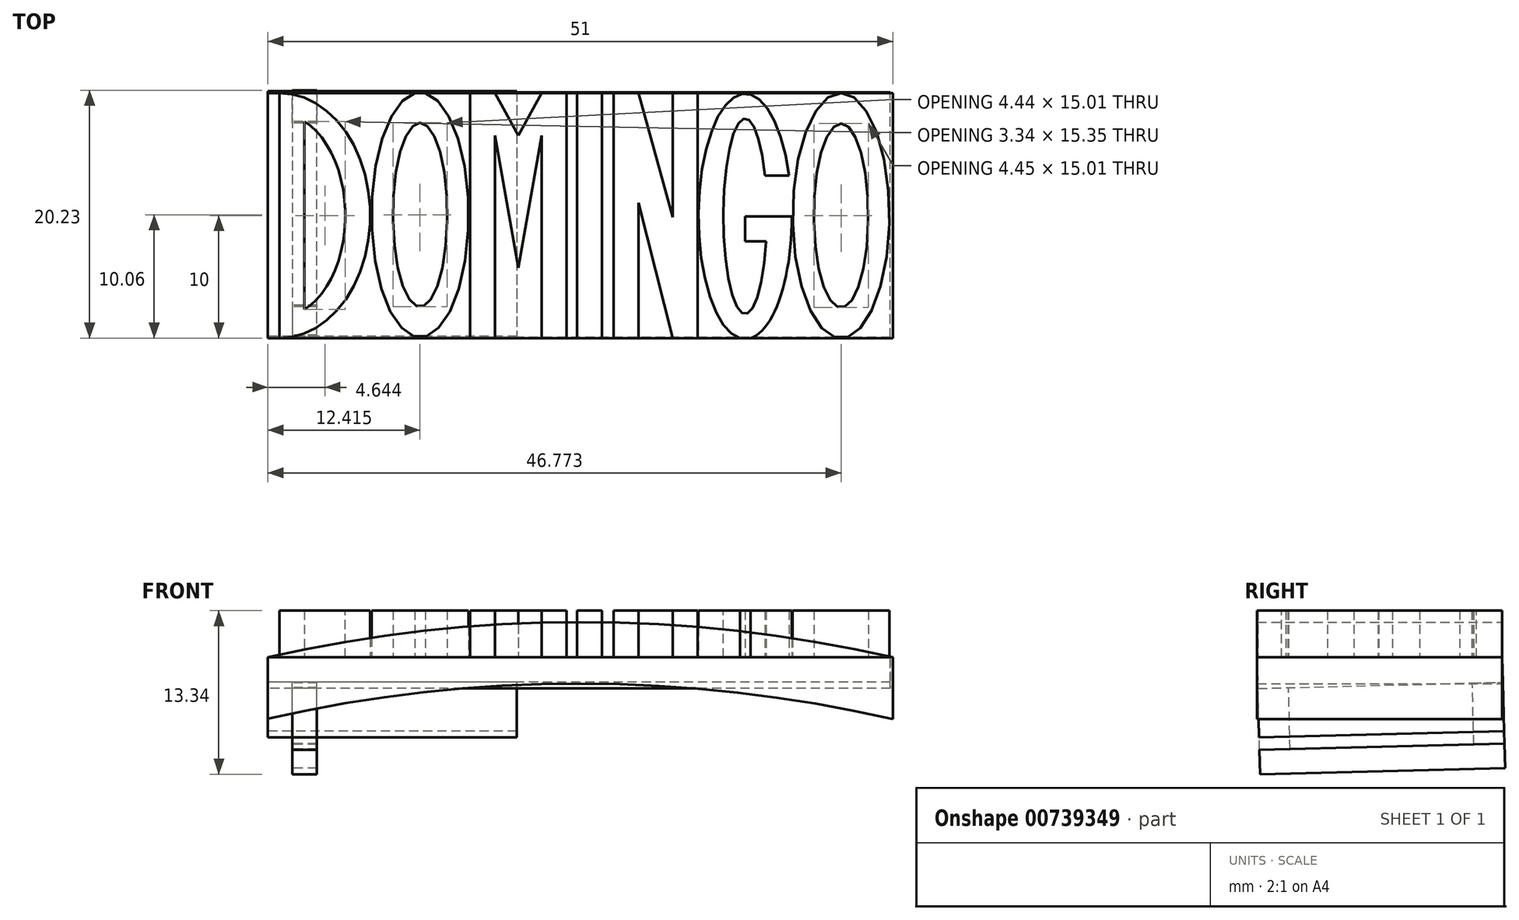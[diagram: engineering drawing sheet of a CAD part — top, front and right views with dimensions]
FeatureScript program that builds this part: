
annotation { "Feature Type Name" : "Feature", "Feature Type Description" : "" }
export const myFeature = defineFeature(function(context is Context, id is Id, definition is map)
    precondition{}
    {
        {
            var Q0;
            Q0=qCreatedBy(makeId("Front.planeOp"),FACE);
            var sketch = newSketch(context, id + "F0", { "sketchPlane" : qUnion([Q0])});
            skArc(sketch, "E0", {"start": v(21, 27.83) * mm, "mid": v(-4.5, 30.73) * mm, "end": v(-30, 27.87) * mm});
            skLineSegment(sketch, "E1", {"start": v(-30, 27.87) * mm, "end": v(-30, 32.87) * mm});
            skLineSegment(sketch, "E2", {"start": v(21, 27.83) * mm, "end": v(21, 32.87) * mm});
            skArc(sketch, "E3", {"start": v(21, 32.87) * mm, "mid": v(-4.5, 35.75) * mm, "end": v(-30, 32.87) * mm});
            skSolve(sketch);
        }
        {
            var Q0;
            Q0=makeQuery(id+"F0.imprint","IMPRINT",FACE,{"disambiguationData":[TD([[makeQuery(id+"F0.imprint","IMPRINT",EDGE,{"derivedFrom":sQuery(id+"F0.wireOp",EDGE,"E0")}),-1.0]])]});
            extrude(context, id + "F1", {"entities" : qUnion([Q0]), "depth" : 20 * mm, "offsetDistance" : 25.4 * mm});
        }
        {
            var Q0;
            Q0=qCreatedBy(makeId("Top.planeOp"),FACE);
            var sketch = newSketch(context, id + "F2", { "sketchPlane" : qUnion([Q0])});
            skLineSegment(sketch, "E4", {"start": v(-23.33, 11.9) * mm, "end": v(-23.33, 4.28) * mm});
            skArc(sketch, "E5", {"start": v(-23.33, 4.28) * mm, "mid": v(-19.37, 8.09) * mm, "end": v(-23.33, 11.9) * mm});
            skSolve(sketch);
        }
        {
            var Q0;
            Q0=makeQuery(id+"F2.imprint","IMPRINT",FACE,{"disambiguationData":[TD([[makeQuery(id+"F2.imprint","IMPRINT",EDGE,{"derivedFrom":sQuery(id+"F2.wireOp",EDGE,"E4")}),1.0]])]});
            extrude(context, id + "F3", {"entities" : qUnion([Q0]), "depth" : 5.08 * mm, "offsetDistance" : 25.4 * mm});
        }
        {
            var Q0;
            Q0=makeQuery(id+"F1.opExtrude","SWEPT_FACE",FACE,{"disambiguationData":[OSD([sQuery(id+"F0.wireOp",EDGE,"E1")])]});
            var sketch = newSketch(context, id + "F4", { "sketchPlane" : qUnion([Q0])});
            skLineSegment(sketch, "E6", {"start": v(20, 32.87) * mm, "end": v(19.94, 30.33) * mm});
            skLineSegment(sketch, "E7", {"start": v(19.94, 30.33) * mm, "end": v(-0.05, 30.84) * mm});
            skLineSegment(sketch, "E8", {"start": v(-0.05, 30.84) * mm, "end": v(0, 32.87) * mm});
            skLineSegment(sketch, "E9", {"start": v(0, 32.87) * mm, "end": v(20, 32.87) * mm});
            skSolve(sketch);
        }
        {
            var Q0;
            Q0 = qSketchRegion(id + "F4", true);
            extrude(context, id + "F5", {"entities" : qUnion([Q0]), "oppositeDirection" : true, "depth" : 50.8 * mm, "offsetDistance" : 25.4 * mm});
        }
        {
            var Q0;
            Q0=makeQuery(id+"F5.opExtrude","SWEPT_FACE",FACE,{"disambiguationData":[OSD([sQuery(id+"F4.wireOp",EDGE,"E9")])]});
            var sketch = newSketch(context, id + "F6", { "sketchPlane" : qUnion([Q0])});
            skLineSegment(sketch, "E10", {"start": v(-29.06, 0) * mm, "end": v(-29.06, -20) * mm});
            skEllipse(sketch, "E11", {"center": v(-29.06, -10) * mm, "majorRadius": 10 * mm, "minorRadius": 7.4 * mm, "majorAxis": v(0, -1)});
            skLineSegment(sketch, "E12", {"start": v(-27.02, -2.33) * mm, "end": v(-27.02, -17.7) * mm});
            skEllipse(sketch, "E13", {"center": v(-29.06, -10) * mm, "majorRadius": 5.37 * mm, "minorRadius": 8.3 * mm, "majorAxis": v(1, 0)});
            skLineSegment(sketch, "E14", {"start": v(-23.69, -10) * mm, "end": v(-21.66, -10) * mm});
            skSolve(sketch);
        }
        {
            var Q0;
            {var subQ0=sQuery(id+"F6.wireOp",EDGE,"E10");Q0=makeQuery(id+"F6.imprint","IMPRINT",FACE,{"disambiguationData":[TD([[makeQuery(id+"F6.imprint","IMPRINT",EDGE,{"derivedFrom":subQ0}),1.0]])]});}
            var Q1;
            {var subQ4=sQuery(id+"F6.wireOp",EDGE,"E12");Q1=makeQuery(id+"F6.imprint","IMPRINT",FACE,{"disambiguationData":[TD([[makeQuery(id+"F6.imprint","IMPRINT",EDGE,{"derivedFrom":subQ4}),-1.0]])]});}
            var Q2;
            {var subQ2=sQuery(id+"F6.wireOp",EDGE,"zUHBSBTi-NJOX-96SZ-FGQs-dRdukynPxQgg");Q2=makeQuery(id+"F6.imprint","IMPRINT",FACE,{"disambiguationData":[TD([[makeQuery(id+"F6.imprint","IMPRINT",EDGE,{"derivedFrom":subQ2}),1.0]])]});}
            var Q3;
            {var subQ0=sQuery(id+"F6.wireOp",EDGE,"zUHBSBTi-NJOX-96SZ-FGQs-dRdukynPxQgg");Q3=makeQuery(id+"F6.imprint","IMPRINT",FACE,{"disambiguationData":[TD([[makeQuery(id+"F6.imprint","IMPRINT",EDGE,{"derivedFrom":subQ0}),-1.0]])]});}
            var Q4;
            {var subQ2=sQuery(id+"F6.wireOp",EDGE,"E14");Q4=makeQuery(id+"F6.imprint","IMPRINT",FACE,{"disambiguationData":[TD([[makeQuery(id+"F6.imprint","IMPRINT",EDGE,{"derivedFrom":subQ2}),1.0]])]});}
            var Q5;
            {var subQ0=sQuery(id+"F6.wireOp",EDGE,"E14");Q5=makeQuery(id+"F6.imprint","IMPRINT",FACE,{"disambiguationData":[TD([[makeQuery(id+"F6.imprint","IMPRINT",EDGE,{"derivedFrom":subQ0}),-1.0]])]});}
            extrude(context, id + "F7", {"entities" : qUnion([Q0, Q1, Q2, Q3, Q4, Q5]), "depth" : 3.8 * mm, "offsetDistance" : 25.4 * mm});
        }
        {
            var Q0;
            Q0=makeQuery(id+"F7.opExtrude","SWEPT_BODY",BODY,{"disambiguationData":[OSD([sQuery(id+"F6.wireOp",EDGE,"E10"),sQuery(id+"F6.wireOp",EDGE,"E11")])]});
            transform(context, id + "F8", {"entities" : qUnion([Q0]), "transformType" : TransformType.TRANSLATION_3D, "dx" : 9.37 * mm, "dy" : -0.15 * mm, "dz" : 0 * mm, "makeCopy" : true});
        }
        {
            var Q0;
            Q0=makeQuery(id+"F8.opPattern","COPY",BODY,{"derivedFrom":makeQuery(id+"F7.opExtrude","SWEPT_BODY",BODY,{"disambiguationData":[OSD([sQuery(id+"F6.wireOp",EDGE,"E10"),sQuery(id+"F6.wireOp",EDGE,"E11")])]}),"instanceName":"1"});
            deleteBodies(context, id + "F9", {"entities" : qUnion([Q0])});
        }
        {
            var Q0;
            Q0=makeQuery(id+"F5.opExtrude","SWEPT_FACE",FACE,{"disambiguationData":[OSD([sQuery(id+"F4.wireOp",EDGE,"E7")])]});
            var sketch = newSketch(context, id + "F10", { "sketchPlane" : qUnion([Q0])});
            skLineSegment(sketch, "E15", {"start": v(-28, 19.17) * mm, "end": v(-26, 19.17) * mm});
            skLineSegment(sketch, "E16", {"start": v(-26, 19.17) * mm, "end": v(-26, 16.67) * mm});
            skLineSegment(sketch, "E17", {"start": v(-26, 16.67) * mm, "end": v(-28, 16.67) * mm});
            skLineSegment(sketch, "E18", {"start": v(-28, 16.67) * mm, "end": v(-28, 19.17) * mm});
            skLineSegment(sketch, "E19", {"start": v(-28, 1.67) * mm, "end": v(-28, -0.83) * mm});
            skLineSegment(sketch, "E20", {"start": v(-28, -0.83) * mm, "end": v(-26, -0.83) * mm});
            skLineSegment(sketch, "E21", {"start": v(-26, -0.83) * mm, "end": v(-26, 1.67) * mm});
            skLineSegment(sketch, "E22", {"start": v(-26, 1.67) * mm, "end": v(-28, 1.67) * mm});
            skLineSegment(sketch, "E23", {"start": v(-26, 1.67) * mm, "end": v(-26, 16.67) * mm});
            skLineSegment(sketch, "E24", {"start": v(-28, 1.67) * mm, "end": v(-28, 16.67) * mm});
            skSolve(sketch);
        }
        {
            var Q0;
            Q0=makeQuery(id+"F10.imprint","IMPRINT",FACE,{"disambiguationData":[TD([[makeQuery(id+"F10.imprint","IMPRINT",EDGE,{"derivedFrom":sQuery(id+"F10.wireOp",EDGE,"E15")}),1.0]])]});
            var Q1;
            Q1=makeQuery(id+"F10.imprint","IMPRINT",FACE,{"disambiguationData":[TD([[makeQuery(id+"F10.imprint","IMPRINT",EDGE,{"derivedFrom":sQuery(id+"F10.wireOp",EDGE,"E19")}),1.0]])]});
            extrude(context, id + "F11", {"entities" : qUnion([Q0, Q1]), "depth" : 5 * mm, "offsetDistance" : 25.4 * mm});
        }
        {
            var Q0;
            Q0=makeQuery(id+"F11.opExtrude","CAP_FACE",FACE,{"disambiguationData":[OSD([sQuery(id+"F10.wireOp",EDGE,"E15"),sQuery(id+"F10.wireOp",EDGE,"E16"),sQuery(id+"F10.wireOp",EDGE,"E17"),sQuery(id+"F10.wireOp",EDGE,"E18")])],"isStart":false});
            var sketch = newSketch(context, id + "F12", { "sketchPlane" : qUnion([Q0])});
            skLineSegment(sketch, "E25", {"start": v(-26, 19.17) * mm, "end": v(-26, -0.83) * mm});
            skLineSegment(sketch, "E26", {"start": v(-26, -0.83) * mm, "end": v(-28, -0.83) * mm});
            skLineSegment(sketch, "E27", {"start": v(-28, -0.83) * mm, "end": v(-28, 19.17) * mm});
            skLineSegment(sketch, "E28", {"start": v(-28, 19.17) * mm, "end": v(-26, 19.17) * mm});
            skSolve(sketch);
        }
        {
            var Q0;
            {var subQ2=sQuery(id+"F12.wireOp",EDGE,"E26");Q0=makeQuery(id+"F12.imprint","IMPRINT",FACE,{"disambiguationData":[TD([[makeQuery(id+"F12.imprint","IMPRINT",EDGE,{"derivedFrom":subQ2}),-1.0]])]});}
            var Q1;
            {var subQ0=sQuery(id+"F12.wireOp",EDGE,"E28");Q1=makeQuery(id+"F12.imprint","IMPRINT",FACE,{"disambiguationData":[TD([[makeQuery(id+"F12.imprint","IMPRINT",EDGE,{"derivedFrom":subQ0}),1.0]])]});}
            extrude(context, id + "F13", {"entities" : qUnion([Q0, Q1]), "depth" : 2 * mm, "offsetDistance" : 25.4 * mm});
        }
        {
            var Q0;
            Q0=makeQuery(id+"F3.opExtrude","SWEPT_BODY",BODY,{"disambiguationData":[OSD([sQuery(id+"F2.wireOp",EDGE,"E4"),sQuery(id+"F2.wireOp",EDGE,"E5")])]});
            deleteBodies(context, id + "F14", {"entities" : qUnion([Q0])});
        }
        {
            var Q0;
            {var subQ2=sQuery(id+"F4.wireOp",EDGE,"E9");var subQ7=makeQuery(id+"F5.opExtrude","CAP_EDGE",EDGE,{"disambiguationData":[OSD([subQ2])],"isStart":false});Q0=makeQuery(id+"F6.imprint","IMPRINT",FACE,{"disambiguationData":[TD([[makeQuery(id+"F6.imprint","IMPRINT",EDGE,{"derivedFrom":subQ7}),1.0]])]});}
            var sketch = newSketch(context, id + "F15", { "sketchPlane" : qUnion([Q0])});
            skEllipse(sketch, "E29", {"center": v(-17.59, -9.94) * mm, "majorRadius": 10 * mm, "minorRadius": 3.95 * mm, "majorAxis": v(0, 1)});
            skEllipse(sketch, "E30", {"center": v(-17.59, -9.94) * mm, "majorRadius": 7.5 * mm, "minorRadius": 2.22 * mm, "majorAxis": v(0, 1)});
            skSolve(sketch);
        }
        {
            var Q0;
            Q0=makeQuery(id+"F15.imprint","IMPRINT",FACE,{"disambiguationData":[TD([[makeQuery(id+"F15.imprint","IMPRINT",EDGE,{"derivedFrom":sQuery(id+"F15.wireOp",EDGE,"E30")}),-1.0]])]});
            extrude(context, id + "F16", {"entities" : qUnion([Q0]), "depth" : 3.8 * mm, "offsetDistance" : 25.4 * mm});
        }
        {
            var Q0;
            Q0=makeQuery(id+"F5.opExtrude","SWEPT_FACE",FACE,{"disambiguationData":[OSD([sQuery(id+"F4.wireOp",EDGE,"E9")])]});
            var sketch = newSketch(context, id + "F17", { "sketchPlane" : qUnion([Q0])});
            skLineSegment(sketch, "E31", {"start": v(-13.5, 0) * mm, "end": v(-13.5, -20) * mm});
            skLineSegment(sketch, "E32", {"start": v(-13.5, -20) * mm, "end": v(-11.47, -20) * mm});
            skLineSegment(sketch, "E33", {"start": v(-11.47, -20) * mm, "end": v(-11.47, -3.47) * mm});
            skLineSegment(sketch, "E34", {"start": v(-11.47, -3.47) * mm, "end": v(-9.56, -14.27) * mm});
            skLineSegment(sketch, "E35", {"start": v(-9.56, -14.27) * mm, "end": v(-7.66, -3.47) * mm});
            skLineSegment(sketch, "E36", {"start": v(-7.66, -3.47) * mm, "end": v(-7.66, -20) * mm});
            skLineSegment(sketch, "E37", {"start": v(-7.66, -20) * mm, "end": v(-5.62, -20) * mm});
            skLineSegment(sketch, "E38", {"start": v(-5.62, -20) * mm, "end": v(-5.62, 0) * mm});
            skLineSegment(sketch, "E39", {"start": v(-5.62, 0) * mm, "end": v(-7.66, 0) * mm});
            skLineSegment(sketch, "E40", {"start": v(-7.66, 0) * mm, "end": v(-9.56, -3.47) * mm});
            skLineSegment(sketch, "E41", {"start": v(-9.56, -3.47) * mm, "end": v(-11.47, 0) * mm});
            skLineSegment(sketch, "E42", {"start": v(-11.47, 0) * mm, "end": v(-13.5, 0) * mm});
            skSolve(sketch);
        }
        {
            var Q0;
            Q0=makeQuery(id+"F17.imprint","IMPRINT",FACE,{"disambiguationData":[TD([[makeQuery(id+"F17.imprint","IMPRINT",EDGE,{"derivedFrom":sQuery(id+"F17.wireOp",EDGE,"E31")}),1.0]])]});
            extrude(context, id + "F18", {"entities" : qUnion([Q0]), "depth" : 3.8 * mm, "offsetDistance" : 25.4 * mm});
        }
        {
            var Q0;
            {var subQ1=sQuery(id+"F4.wireOp",EDGE,"E9");Q0=makeQuery(id+"F18.boolean.opBoolean","SPLIT",FACE,{"disambiguationData":[TD([makeQuery(id+"F18.opExtrude","SWEPT_FACE",FACE,{"disambiguationData":[OSD([sQuery(id+"F17.wireOp",EDGE,"E38")])]})])],"derivedFrom":makeQuery(id+"F5.opExtrude","SWEPT_FACE",FACE,{"disambiguationData":[OSD([subQ1])]})});}
            var sketch = newSketch(context, id + "F19", { "sketchPlane" : qUnion([Q0])});
            skLineSegment(sketch, "E43", {"start": v(-4.77, 0) * mm, "end": v(-4.77, -20) * mm});
            skLineSegment(sketch, "E44", {"start": v(-4.77, -20) * mm, "end": v(-2.74, -20) * mm});
            skLineSegment(sketch, "E45", {"start": v(-2.74, -20) * mm, "end": v(-2.74, 0) * mm});
            skLineSegment(sketch, "E46", {"start": v(-2.74, 0) * mm, "end": v(-4.77, 0) * mm});
            skSolve(sketch);
        }
        {
            var Q0;
            Q0=makeQuery(id+"F19.imprint","IMPRINT",FACE,{"disambiguationData":[TD([[makeQuery(id+"F19.imprint","IMPRINT",EDGE,{"derivedFrom":sQuery(id+"F19.wireOp",EDGE,"E43")}),1.0]])]});
            extrude(context, id + "F20", {"entities" : qUnion([Q0]), "depth" : 3.8 * mm, "offsetDistance" : 25.4 * mm});
        }
        {
            var Q0;
            Q0=makeQuery(id+"F5.opExtrude","SWEPT_FACE",FACE,{"disambiguationData":[OSD([sQuery(id+"F4.wireOp",EDGE,"E9")])]});
            var sketch = newSketch(context, id + "F21", { "sketchPlane" : qUnion([Q0])});
            skLineSegment(sketch, "E47", {"start": v(-1.78, 0) * mm, "end": v(0.26, 0) * mm});
            skLineSegment(sketch, "E48", {"start": v(-1.78, -20) * mm, "end": v(0.26, -20) * mm});
            skLineSegment(sketch, "E49", {"start": v(-1.78, 0) * mm, "end": v(-1.78, -20) * mm});
            skLineSegment(sketch, "E50", {"start": v(3.05, -20) * mm, "end": v(5.08, -20) * mm});
            skLineSegment(sketch, "E51", {"start": v(3.05, 0) * mm, "end": v(5.08, 0) * mm});
            skLineSegment(sketch, "E52", {"start": v(5.08, 0) * mm, "end": v(5.08, -20) * mm});
            skLineSegment(sketch, "E53", {"start": v(0.26, -20) * mm, "end": v(0.26, -8.96) * mm});
            skLineSegment(sketch, "E54", {"start": v(0.26, -8.96) * mm, "end": v(3.05, -20) * mm});
            skLineSegment(sketch, "E55", {"start": v(3.05, 0) * mm, "end": v(3.05, -10.13) * mm});
            skLineSegment(sketch, "E56", {"start": v(3.05, -10.13) * mm, "end": v(0.26, 0) * mm});
            skSolve(sketch);
        }
        {
            var Q0;
            Q0=makeQuery(id+"F21.imprint","IMPRINT",FACE,{"disambiguationData":[TD([[makeQuery(id+"F21.imprint","IMPRINT",EDGE,{"derivedFrom":sQuery(id+"F21.wireOp",EDGE,"E47")}),1.0]])]});
            extrude(context, id + "F22", {"entities" : qUnion([Q0]), "depth" : 3.8 * mm, "offsetDistance" : 25.4 * mm});
        }
        {
            var Q0;
            {var subQ1=sQuery(id+"F4.wireOp",EDGE,"E9");Q0=makeQuery(id+"F22.boolean.opBoolean","SPLIT",FACE,{"disambiguationData":[TD([makeQuery(id+"F22.opExtrude","SWEPT_FACE",FACE,{"disambiguationData":[OSD([sQuery(id+"F21.wireOp",EDGE,"E52")])]})])],"derivedFrom":makeQuery(id+"F5.opExtrude","SWEPT_FACE",FACE,{"disambiguationData":[OSD([subQ1])]})});}
            var sketch = newSketch(context, id + "F23", { "sketchPlane" : qUnion([Q0])});
            skEllipse(sketch, "E57", {"center": v(8.95, -10.06) * mm, "majorRadius": 10 * mm, "minorRadius": 3.81 * mm, "majorAxis": v(0, 1)});
            skEllipse(sketch, "E58", {"center": v(8.95, -10.06) * mm, "majorRadius": 7.97 * mm, "minorRadius": 1.78 * mm, "majorAxis": v(0, 1)});
            skLineSegment(sketch, "E59", {"start": v(10.73, -10.06) * mm, "end": v(12.76, -10.06) * mm});
            skLineSegment(sketch, "E60", {"start": v(8.95, -0.06) * mm, "end": v(8.95, -2.1) * mm});
            skLineSegment(sketch, "E61", {"start": v(8.95, -10.06) * mm, "end": v(10.73, -10.06) * mm});
            skLineSegment(sketch, "E62", {"start": v(8.95, -10.06) * mm, "end": v(8.95, -12.1) * mm});
            skLineSegment(sketch, "E63", {"start": v(8.95, -12.1) * mm, "end": v(10.67, -12.1) * mm});
            skLineSegment(sketch, "E64", {"start": v(12.54, -6.74) * mm, "end": v(10.56, -6.74) * mm});
            skLineSegment(sketch, "E65", {"start": v(8.95, -0.06) * mm, "end": v(8.95, -20.06) * mm});
            skSolve(sketch);
        }
        {
            var Q0;
            {var subQ0=sQuery(id+"F23.wireOp",EDGE,"E60");Q0=makeQuery(id+"F23.imprint","IMPRINT",FACE,{"disambiguationData":[TD([[makeQuery(id+"F23.imprint","IMPRINT",EDGE,{"derivedFrom":subQ0}),1.0]])]});}
            var Q1;
            {var subQ0=sQuery(id+"F23.wireOp",EDGE,"E59");Q1=makeQuery(id+"F23.imprint","IMPRINT",FACE,{"disambiguationData":[TD([[makeQuery(id+"F23.imprint","IMPRINT",EDGE,{"derivedFrom":subQ0}),-1.0]])]});}
            var Q2;
            {var subQ0=sQuery(id+"F23.wireOp",EDGE,"E61");Q2=makeQuery(id+"F23.imprint","IMPRINT",FACE,{"disambiguationData":[TD([[makeQuery(id+"F23.imprint","IMPRINT",EDGE,{"derivedFrom":subQ0}),-1.0]])]});}
            var Q3;
            {var subQ0=sQuery(id+"F23.wireOp",EDGE,"E65");var subQ3=sQuery(id+"F23.wireOp",EDGE,"E58");var subQ4=makeQuery(id+"F23.imprint","INTERSECT",VERTEX,{"disambiguationData":[OD(0.0)],"derivedFrom":[subQ3,subQ0]});Q3=makeQuery(id+"F23.imprint","IMPRINT",FACE,{"disambiguationData":[TD([[makeQuery(id+"F23.imprint","IMPRINT",EDGE,{"disambiguationData":[TD([[subQ4,1.0]])],"derivedFrom":subQ3}),-1.0]])]});}
            var Q4;
            {var subQ7=sQuery(id+"F23.wireOp",EDGE,"E64");Q4=makeQuery(id+"F23.imprint","IMPRINT",FACE,{"disambiguationData":[TD([[makeQuery(id+"F23.imprint","IMPRINT",EDGE,{"derivedFrom":subQ7}),-1.0]])]});}
            extrude(context, id + "F24", {"entities" : qUnion([Q0, Q1, Q2, Q3, Q4]), "depth" : 3.8 * mm, "offsetDistance" : 25.4 * mm});
        }
        {
            var Q0;
            Q0=makeQuery(id+"F5.opExtrude","SWEPT_FACE",FACE,{"disambiguationData":[OSD([sQuery(id+"F4.wireOp",EDGE,"E9")])]});
            var sketch = newSketch(context, id + "F25", { "sketchPlane" : qUnion([Q0])});
            skEllipse(sketch, "E66", {"center": v(16.77, -10) * mm, "majorRadius": 10 * mm, "minorRadius": 3.95 * mm, "majorAxis": v(0, 1)});
            skPoint(sketch, "E66.centerSnap0", {"position": v(20.8, -10) * mm});
            skEllipse(sketch, "E67", {"center": v(16.77, -10) * mm, "majorRadius": 7.5 * mm, "minorRadius": 2.22 * mm, "majorAxis": v(0, 1)});
            skSolve(sketch);
        }
        {
            var Q0;
            Q0=makeQuery(id+"F25.imprint","IMPRINT",FACE,{"disambiguationData":[TD([[makeQuery(id+"F25.imprint","IMPRINT",EDGE,{"derivedFrom":sQuery(id+"F25.wireOp",EDGE,"E67")}),-1.0]])]});
            extrude(context, id + "F26", {"entities" : qUnion([Q0]), "depth" : 3.8 * mm, "offsetDistance" : 25.4 * mm});
        }
        {
            var Q0;
            Q0=makeQuery(id+"F5.opExtrude","SWEPT_FACE",FACE,{"disambiguationData":[OSD([sQuery(id+"F4.wireOp",EDGE,"E7")])]});
            var sketch = newSketch(context, id + "F27", { "sketchPlane" : qUnion([Q0])});
            skLineSegment(sketch, "E68", {"start": v(-30, 19.17) * mm, "end": v(-30, -0.83) * mm});
            skLineSegment(sketch, "E69", {"start": v(-30, -0.83) * mm, "end": v(-9.68, -0.83) * mm});
            skLineSegment(sketch, "E70", {"start": v(-9.68, -0.83) * mm, "end": v(-9.68, 19.17) * mm});
            skLineSegment(sketch, "E71", {"start": v(-9.68, 19.17) * mm, "end": v(-30, 19.17) * mm});
            skSolve(sketch);
        }
        {
            var Q0;
            Q0 = qSketchRegion(id + "F27", true);
            extrude(context, id + "F28", {"entities" : qUnion([Q0]), "depth" : 4 * mm, "offsetDistance" : 25.4 * mm});
        }
    });
